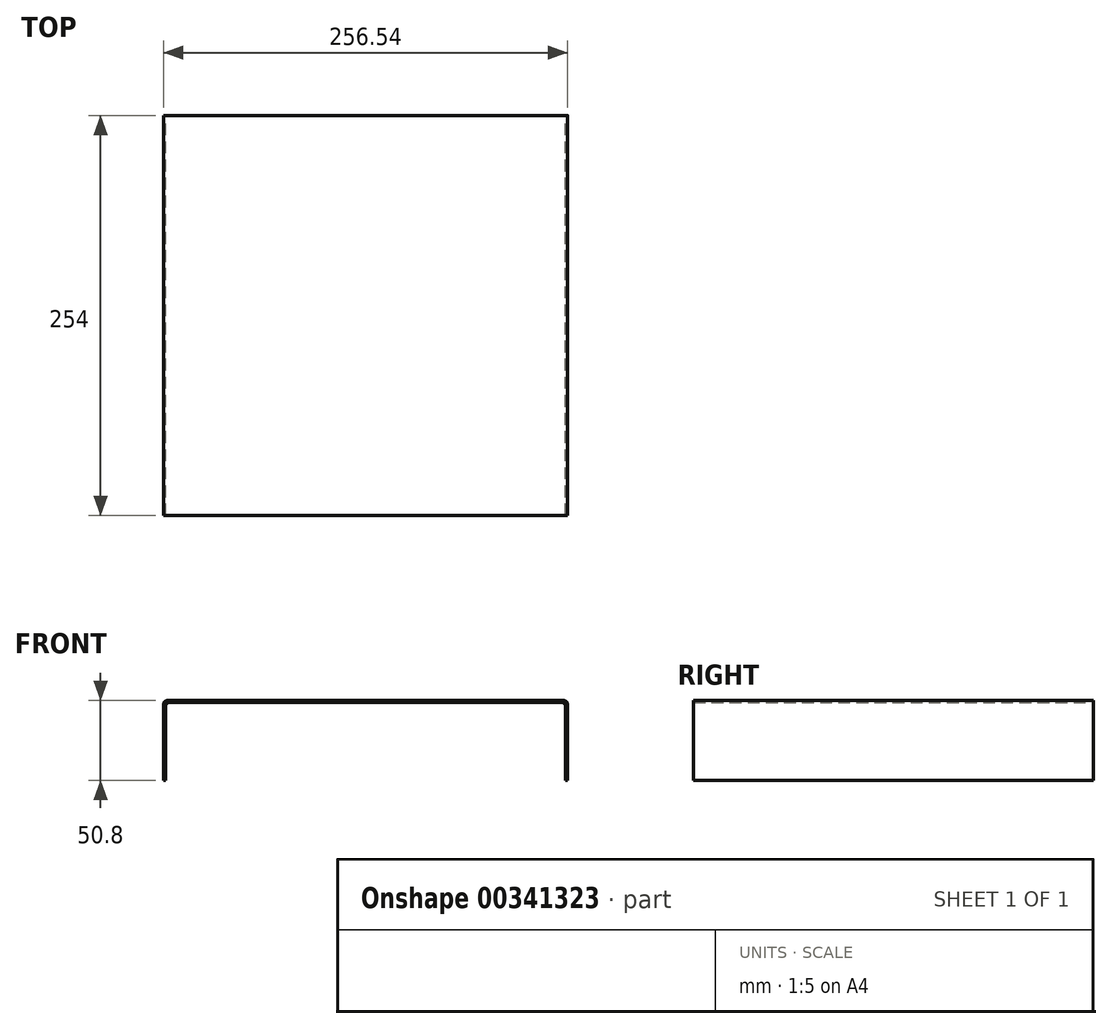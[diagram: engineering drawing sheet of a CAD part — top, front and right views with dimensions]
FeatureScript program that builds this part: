
annotation { "Feature Type Name" : "Feature", "Feature Type Description" : "" }
export const myFeature = defineFeature(function(context is Context, id is Id, definition is map)
    precondition{}
    {
        {
            var Q0;
            Q0=qCreatedBy(makeId("Front.planeOp"),FACE);
            var sketch = newSketch(context, id + "F0", { "sketchPlane" : qUnion([Q0])});
            skLineSegment(sketch, "E0.bottom", {"start": v(128.27, 25.4) * mm, "end": v(-128.27, 25.4) * mm});
            skLineSegment(sketch, "E0.top", {"start": v(128.27, -25.4) * mm, "end": v(-128.27, -25.4) * mm});
            skLineSegment(sketch, "E0.left", {"start": v(128.27, 25.4) * mm, "end": v(128.27, -25.4) * mm});
            skLineSegment(sketch, "E0.right", {"start": v(-128.27, 25.4) * mm, "end": v(-128.27, -25.4) * mm});
            skPoint(sketch, "E0.middle", {"position": v(0, 0) * mm});
            skSolve(sketch);
        }
        {
            var Q0;
            Q0 = qSketchRegion(id + "F0", true);
            extrude(context, id + "F1", {"entities" : qUnion([Q0]), "depth" : 254 * mm});
        }
        {
            var Q0;
            Q0=makeQuery(id+"F1.opExtrude","CAP_FACE",FACE,{"disambiguationData":[OSD([sQuery(id+"F0.wireOp",EDGE,"E0.bottom"),sQuery(id+"F0.wireOp",EDGE,"E0.top"),sQuery(id+"F0.wireOp",EDGE,"E0.left"),sQuery(id+"F0.wireOp",EDGE,"E0.right")])],"isStart":false});
            var Q1;
            Q1=makeQuery(id+"F1.opExtrude","SWEPT_FACE",FACE,{"disambiguationData":[OSD([sQuery(id+"F0.wireOp",EDGE,"E0.top")])]});
            var Q2;
            Q2=makeQuery(id+"F1.opExtrude","CAP_FACE",FACE,{"disambiguationData":[OSD([sQuery(id+"F0.wireOp",EDGE,"E0.bottom"),sQuery(id+"F0.wireOp",EDGE,"E0.top"),sQuery(id+"F0.wireOp",EDGE,"E0.left"),sQuery(id+"F0.wireOp",EDGE,"E0.right")])],"isStart":true});
            shell(context, id + "F2", {"entities" : qUnion([Q0, Q1, Q2]), "thickness" : 1.27 * mm});
        }
        {
            var Q0;
            Q0=makeQuery(id+"F2.opShell","OFFSET_EDGE",EDGE,{"disambiguationData":[OSD([sQuery(id+"F0.wireOp",EDGE,"E0.bottom"),sQuery(id+"F0.wireOp",EDGE,"E0.right")])]});
            var Q1;
            Q1=makeQuery(id+"F2.opShell","OFFSET_EDGE",EDGE,{"disambiguationData":[OSD([sQuery(id+"F0.wireOp",EDGE,"E0.bottom"),sQuery(id+"F0.wireOp",EDGE,"E0.left")])]});
            var Q2;
            Q2=makeQuery(id+"F1.opExtrude","SWEPT_EDGE",EDGE,{"disambiguationData":[OSD([sQuery(id+"F0.wireOp",EDGE,"E0.bottom"),sQuery(id+"F0.wireOp",EDGE,"E0.left")])]});
            var Q3;
            Q3=makeQuery(id+"F1.opExtrude","SWEPT_EDGE",EDGE,{"disambiguationData":[OSD([sQuery(id+"F0.wireOp",EDGE,"E0.bottom"),sQuery(id+"F0.wireOp",EDGE,"E0.right")])]});
            fillet(context, id + "F3", {"entities" : qUnion([Q0, Q1, Q2, Q3]), "radius" : 2.54 * mm, "tangentPropagation" : true, "allowEdgeOverflow" : false});
        }
    });
